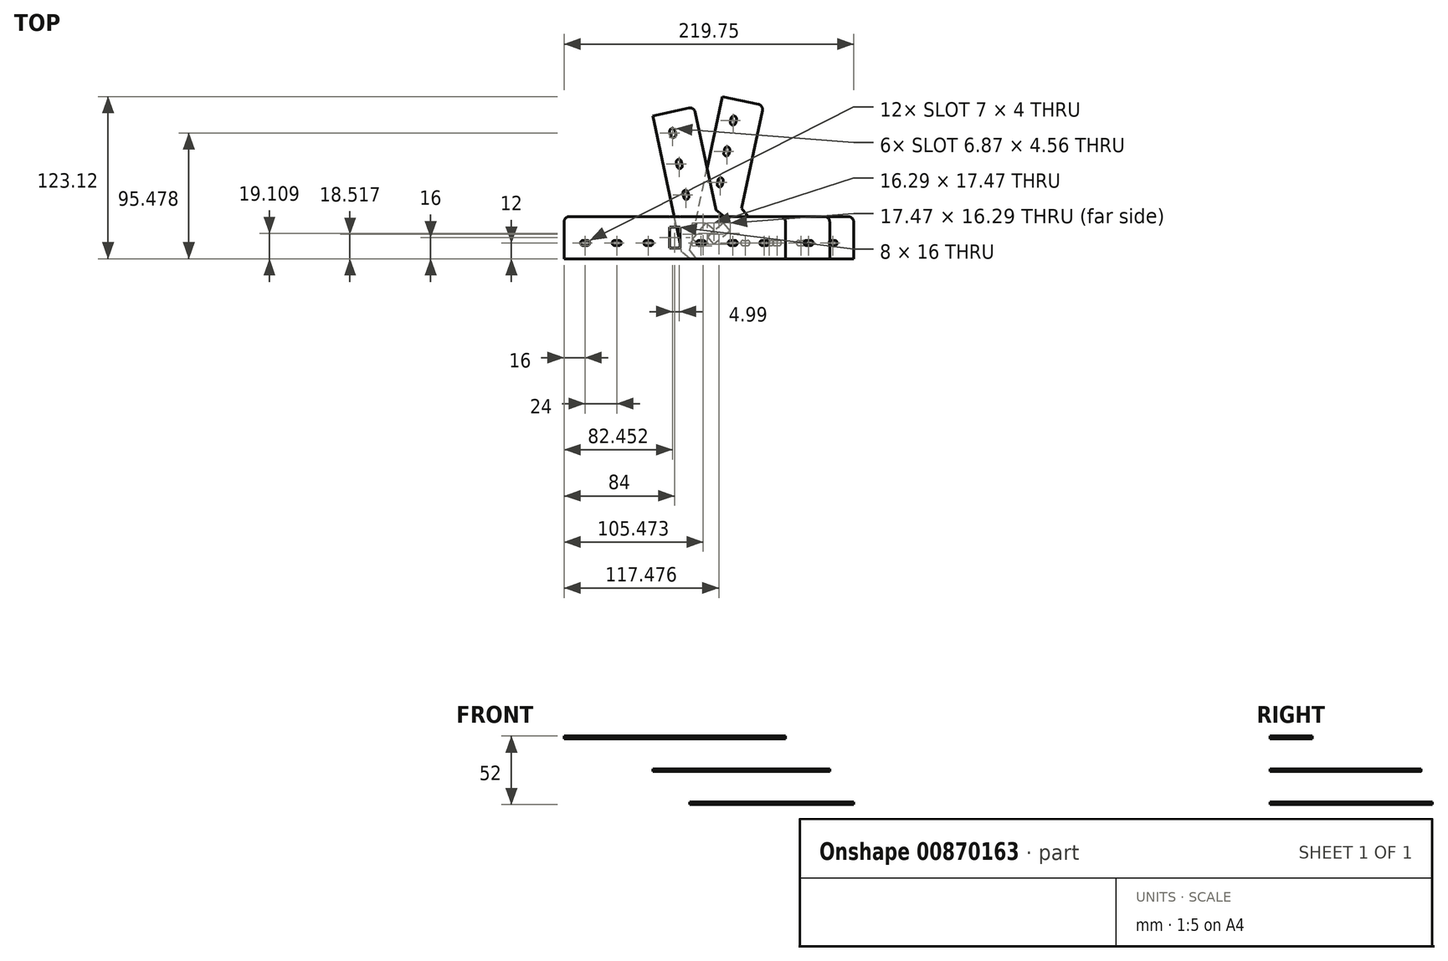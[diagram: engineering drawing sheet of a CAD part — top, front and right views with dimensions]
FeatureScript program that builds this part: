
annotation { "Feature Type Name" : "Feature", "Feature Type Description" : "" }
export const myFeature = defineFeature(function(context is Context, id is Id, definition is map)
    precondition{}
    {
        {
            var Q0;
            Q0=qCreatedBy(makeId("Top.planeOp"),FACE);
            var sketch = newSketch(context, id + "F0", { "sketchPlane" : qUnion([Q0])});
            skLineSegment(sketch, "E0", {"start": v(39.7, 32.14) * mm, "end": v(42.21, 29.03) * mm});
            skLineSegment(sketch, "E1", {"start": v(42.21, 29.03) * mm, "end": v(29.78, 18.97) * mm});
            skLineSegment(sketch, "E2", {"start": v(29.78, 18.97) * mm, "end": v(27.26, 22.07) * mm});
            skLineSegment(sketch, "E3", {"start": v(27.26, 22.07) * mm, "end": v(13.72, 11.1) * mm, "construction": true});
            skLineSegment(sketch, "E4", {"start": v(9.88, 8) * mm, "end": v(16.24, 8) * mm, "construction": true});
            skLineSegment(sketch, "E5", {"start": v(135.75, 8) * mm, "end": v(135.75, 36) * mm});
            skLineSegment(sketch, "E6", {"start": v(131.75, 40) * mm, "end": v(55.75, 40) * mm});
            skLineSegment(sketch, "E7", {"start": v(135.75, 8) * mm, "end": v(135.75, 0) * mm, "construction": true});
            skLineSegment(sketch, "E8", {"start": v(135.75, 0) * mm, "end": v(0, 0) * mm, "construction": true});
            skLineSegment(sketch, "E9", {"start": v(0, 0) * mm, "end": v(9.88, 8) * mm, "construction": true});
            skLineSegment(sketch, "E10", {"start": v(119.75, 40) * mm, "end": v(119.75, 0) * mm, "construction": true});
            skLineSegment(sketch, "E11", {"start": v(118.25, 22) * mm, "end": v(121.25, 22) * mm});
            skArc(sketch, "E12", {"start": v(118.25, 22) * mm, "mid": v(116.25, 20) * mm, "end": v(118.25, 18) * mm});
            skLineSegment(sketch, "E13", {"start": v(118.25, 18) * mm, "end": v(121.25, 18) * mm});
            skArc(sketch, "E14", {"start": v(121.25, 18) * mm, "mid": v(123.25, 20) * mm, "end": v(121.25, 22) * mm});
            skLineSegment(sketch, "E15", {"start": v(118.25, 20) * mm, "end": v(119.75, 20) * mm, "construction": true});
            skLineSegment(sketch, "E16", {"start": v(119.75, 20) * mm, "end": v(121.25, 20) * mm, "construction": true});
            skArc(sketch, "E17.1.0.0", {"start": v(94.25, 22) * mm, "mid": v(92.25, 20) * mm, "end": v(94.25, 18) * mm});
            skLineSegment(sketch, "E17.1.0.1", {"start": v(94.25, 22) * mm, "end": v(97.25, 22) * mm});
            skArc(sketch, "E17.1.0.2", {"start": v(97.25, 18) * mm, "mid": v(99.25, 20) * mm, "end": v(97.25, 22) * mm});
            skLineSegment(sketch, "E17.1.0.3", {"start": v(94.25, 18) * mm, "end": v(97.25, 18) * mm});
            skArc(sketch, "E17.2.0.0", {"start": v(70.25, 22) * mm, "mid": v(68.25, 20) * mm, "end": v(70.25, 18) * mm});
            skLineSegment(sketch, "E17.2.0.1", {"start": v(70.25, 22) * mm, "end": v(73.25, 22) * mm});
            skArc(sketch, "E17.2.0.2", {"start": v(73.25, 18) * mm, "mid": v(75.25, 20) * mm, "end": v(73.25, 22) * mm});
            skLineSegment(sketch, "E17.2.0.3", {"start": v(70.25, 18) * mm, "end": v(73.25, 18) * mm});
            skLineSegment(sketch, "E17.direction1", {"start": v(94.25, 18) * mm, "end": v(118.25, 18) * mm, "construction": true});
            skPoint(sketch, "E18.visualSharp", {"position": v(135.75, 40) * mm});
            skArc(sketch, "E18.filletArc", {"start": v(135.75, 36) * mm, "mid": v(134.58, 38.83) * mm, "end": v(131.75, 40) * mm});
            skLineSegment(sketch, "E19", {"start": v(53.23, 43.1) * mm, "end": v(39.7, 32.14) * mm, "construction": true});
            skLineSegment(sketch, "E20", {"start": v(0, 0) * mm, "end": v(2.05, 9.66) * mm, "construction": true});
            skLineSegment(sketch, "E21", {"start": v(2.05, 9.66) * mm, "end": v(9.88, 8) * mm, "construction": true});
            skLineSegment(sketch, "E22", {"start": v(9.88, 8) * mm, "end": v(9.88, 0) * mm, "construction": true});
            skLineSegment(sketch, "E23", {"start": v(9.88, 0) * mm, "end": v(0, 0) * mm, "construction": true});
            skLineSegment(sketch, "E24", {"start": v(16.24, 8) * mm, "end": v(13.72, 11.1) * mm});
            skLineSegment(sketch, "E25", {"start": v(16.24, 8) * mm, "end": v(135.75, 8) * mm});
            skLineSegment(sketch, "E26", {"start": v(13.72, 11.1) * mm, "end": v(9.88, 8) * mm, "construction": true});
            skLineSegment(sketch, "E27", {"start": v(55.75, 40) * mm, "end": v(53.23, 43.1) * mm});
            skLineSegment(sketch, "E28.MirrorCS", {"start": v(37.2, 88.45) * mm, "end": v(37.83, 91.38) * mm});
            skLineSegment(sketch, "E29.MirrorCS", {"start": v(41.12, 87.62) * mm, "end": v(41.74, 90.55) * mm});
            skLineSegment(sketch, "E30.MirrorCS", {"start": v(32.21, 64.97) * mm, "end": v(32.84, 67.9) * mm});
            skLineSegment(sketch, "E31.MirrorCS", {"start": v(42.2, 111.93) * mm, "end": v(42.82, 114.86) * mm});
            skLineSegment(sketch, "E32.MirrorCS", {"start": v(46.1, 111.1) * mm, "end": v(46.73, 114.03) * mm});
            skLineSegment(sketch, "E33.MirrorCS", {"start": v(36.13, 64.14) * mm, "end": v(36.75, 67.08) * mm});
            skArc(sketch, "E34.MirrorCS", {"start": v(37.83, 91.38) * mm, "mid": v(40.2, 92.92) * mm, "end": v(41.74, 90.55) * mm});
            skLineSegment(sketch, "E35.MirrorCS", {"start": v(24.74, 25.18) * mm, "end": v(27.26, 22.07) * mm});
            skArc(sketch, "E36.MirrorCS", {"start": v(41.12, 87.62) * mm, "mid": v(38.74, 86.08) * mm, "end": v(37.2, 88.45) * mm});
            skLineSegment(sketch, "E37.MirrorCS", {"start": v(36.05, 131.12) * mm, "end": v(63.44, 125.3) * mm});
            skPoint(sketch, "E38.MirrorP", {"position": v(67.35, 124.47) * mm});
            skLineSegment(sketch, "E39.MirrorCS", {"start": v(37.18, 35.25) * mm, "end": v(24.74, 25.18) * mm});
            skArc(sketch, "E40.MirrorCS", {"start": v(46.1, 111.1) * mm, "mid": v(43.73, 109.55) * mm, "end": v(42.2, 111.93) * mm});
            skLineSegment(sketch, "E41.MirrorCS", {"start": v(66.52, 120.56) * mm, "end": v(50.72, 46.22) * mm});
            skLineSegment(sketch, "E42.MirrorCS", {"start": v(11.2, 14.22) * mm, "end": v(13.72, 11.1) * mm});
            skLineSegment(sketch, "E43.MirrorCS", {"start": v(50.72, 46.22) * mm, "end": v(53.23, 43.1) * mm});
            skLineSegment(sketch, "E44.MirrorCS", {"start": v(11.2, 14.22) * mm, "end": v(36.05, 131.12) * mm});
            skArc(sketch, "E45.MirrorCS", {"start": v(63.44, 125.3) * mm, "mid": v(65.96, 123.57) * mm, "end": v(66.52, 120.56) * mm});
            skLineSegment(sketch, "E46.MirrorCS", {"start": v(39.7, 32.14) * mm, "end": v(37.18, 35.25) * mm});
            skArc(sketch, "E47.MirrorCS", {"start": v(36.13, 64.14) * mm, "mid": v(33.75, 62.6) * mm, "end": v(32.21, 64.97) * mm});
            skArc(sketch, "E48.MirrorCS", {"start": v(42.82, 114.86) * mm, "mid": v(45.19, 116.4) * mm, "end": v(46.73, 114.03) * mm});
            skArc(sketch, "E49.MirrorCS", {"start": v(32.84, 67.9) * mm, "mid": v(35.2, 69.45) * mm, "end": v(36.75, 67.08) * mm});
            skSolve(sketch);
        }
        {
            var Q0;
            Q0 = qSketchRegion(id + "F0", true);
            extrude(context, id + "F1", {"entities" : qUnion([Q0]), "depth" : 2 * mm, "offsetDistance" : 25 * mm});
        }
        {
            var Q0;
            Q0=qCreatedBy(makeId("Top.planeOp"),FACE);
            cPlane(context, id + "F2", {"entities" : qUnion([Q0]), "cplaneType" : CPlaneType.OFFSET, "offset" : 25 * mm, "width" : 150 * mm, "height" : 150 * mm});
        }
        {
            var Q0;
            Q0=qCreatedBy(id+"F2.planeOp",FACE);
            var sketch = newSketch(context, id + "F3", { "sketchPlane" : qUnion([Q0])});
            skLineSegment(sketch, "E50", {"start": v(0, 0) * mm, "end": v(117.54, 0) * mm, "construction": true});
            skLineSegment(sketch, "E51", {"start": v(117.54, 0) * mm, "end": v(117.54, 8) * mm, "construction": true});
            skLineSegment(sketch, "E52", {"start": v(11.63, 8) * mm, "end": v(8.52, 10.52) * mm});
            skLineSegment(sketch, "E53", {"start": v(11.63, 8) * mm, "end": v(117.54, 8) * mm});
            skLineSegment(sketch, "E54", {"start": v(117.54, 8) * mm, "end": v(117.54, 36) * mm});
            skArc(sketch, "E55", {"start": v(117.54, 36) * mm, "mid": v(116.37, 38.83) * mm, "end": v(113.54, 40) * mm});
            skLineSegment(sketch, "E56", {"start": v(113.54, 40) * mm, "end": v(37.54, 40) * mm});
            skLineSegment(sketch, "E57", {"start": v(37.54, 40) * mm, "end": v(34.43, 42.52) * mm});
            skLineSegment(sketch, "E58", {"start": v(34.43, 42.52) * mm, "end": v(26.5, 32.73) * mm, "construction": true});
            skLineSegment(sketch, "E59", {"start": v(26.5, 32.73) * mm, "end": v(29.62, 30.22) * mm});
            skLineSegment(sketch, "E60", {"start": v(29.62, 30.22) * mm, "end": v(19.55, 17.78) * mm});
            skLineSegment(sketch, "E61", {"start": v(19.55, 17.78) * mm, "end": v(16.44, 20.3) * mm});
            skLineSegment(sketch, "E62", {"start": v(16.44, 20.3) * mm, "end": v(8.52, 10.52) * mm, "construction": true});
            skLineSegment(sketch, "E63", {"start": v(8.52, 10.52) * mm, "end": v(6.48, 8) * mm, "construction": true});
            skLineSegment(sketch, "E64", {"start": v(6.48, 8) * mm, "end": v(0, 0) * mm, "construction": true});
            skLineSegment(sketch, "E65", {"start": v(0, 0) * mm, "end": v(-1.35, 6.34) * mm, "construction": true});
            skLineSegment(sketch, "E66", {"start": v(-1.35, 6.34) * mm, "end": v(6.48, 8) * mm, "construction": true});
            skLineSegment(sketch, "E67", {"start": v(6.48, 8) * mm, "end": v(6.48, 0) * mm, "construction": true});
            skLineSegment(sketch, "E68", {"start": v(6.48, 0) * mm, "end": v(0, 0) * mm, "construction": true});
            skLineSegment(sketch, "E69", {"start": v(101.54, 0) * mm, "end": v(101.54, 40) * mm, "construction": true});
            skLineSegment(sketch, "E70", {"start": v(101.54, 20) * mm, "end": v(100.04, 20) * mm, "construction": true});
            skLineSegment(sketch, "E71", {"start": v(101.54, 20) * mm, "end": v(103.04, 20) * mm, "construction": true});
            skArc(sketch, "E72", {"start": v(100.04, 18) * mm, "mid": v(98.04, 20) * mm, "end": v(100.04, 22) * mm});
            skArc(sketch, "E73", {"start": v(103.04, 22) * mm, "mid": v(105.04, 20) * mm, "end": v(103.04, 18) * mm});
            skLineSegment(sketch, "E74", {"start": v(100.04, 22) * mm, "end": v(103.04, 22) * mm});
            skLineSegment(sketch, "E75", {"start": v(100.04, 18) * mm, "end": v(103.04, 18) * mm});
            skArc(sketch, "E76.1.0.0", {"start": v(76.04, 18) * mm, "mid": v(74.04, 20) * mm, "end": v(76.04, 22) * mm});
            skLineSegment(sketch, "E76.1.0.1", {"start": v(76.04, 22) * mm, "end": v(79.04, 22) * mm});
            skArc(sketch, "E76.1.0.2", {"start": v(79.04, 22) * mm, "mid": v(81.04, 20) * mm, "end": v(79.04, 18) * mm});
            skLineSegment(sketch, "E76.1.0.3", {"start": v(76.04, 18) * mm, "end": v(79.04, 18) * mm});
            skArc(sketch, "E76.2.0.0", {"start": v(52.04, 18) * mm, "mid": v(50.04, 20) * mm, "end": v(52.04, 22) * mm});
            skLineSegment(sketch, "E76.2.0.1", {"start": v(52.04, 22) * mm, "end": v(55.04, 22) * mm});
            skArc(sketch, "E76.2.0.2", {"start": v(55.04, 22) * mm, "mid": v(57.04, 20) * mm, "end": v(55.04, 18) * mm});
            skLineSegment(sketch, "E76.2.0.3", {"start": v(52.04, 18) * mm, "end": v(55.04, 18) * mm});
            skLineSegment(sketch, "E76.direction1", {"start": v(100.04, 18) * mm, "end": v(76.04, 18) * mm, "construction": true});
            skLineSegment(sketch, "E77.MirrorCS", {"start": v(5.4, 13.03) * mm, "end": v(8.52, 10.52) * mm});
            skLineSegment(sketch, "E78.MirrorCS", {"start": v(-3.2, 101.6) * mm, "end": v(-3.82, 104.53) * mm});
            skLineSegment(sketch, "E79.MirrorCS", {"start": v(6.79, 54.64) * mm, "end": v(6.16, 57.58) * mm});
            skLineSegment(sketch, "E80.MirrorCS", {"start": v(10.7, 55.48) * mm, "end": v(10.08, 58.4) * mm});
            skLineSegment(sketch, "E81.MirrorCS", {"start": v(1.8, 78.12) * mm, "end": v(1.17, 81.05) * mm});
            skLineSegment(sketch, "E82.MirrorCS", {"start": v(0.72, 102.43) * mm, "end": v(0.1, 105.36) * mm});
            skLineSegment(sketch, "E83.MirrorCS", {"start": v(5.7, 78.95) * mm, "end": v(5.09, 81.89) * mm});
            skLineSegment(sketch, "E84.MirrorCS", {"start": v(13.33, 22.82) * mm, "end": v(16.44, 20.3) * mm});
            skLineSegment(sketch, "E85.MirrorCS", {"start": v(26.5, 32.73) * mm, "end": v(23.4, 35.25) * mm});
            skLineSegment(sketch, "E86.MirrorCS", {"start": v(31.32, 45.03) * mm, "end": v(34.43, 42.52) * mm});
            skArc(sketch, "E87.MirrorCS", {"start": v(0.1, 105.36) * mm, "mid": v(-2.28, 106.9) * mm, "end": v(-3.82, 104.53) * mm});
            skArc(sketch, "E88.MirrorCS", {"start": v(5.09, 81.89) * mm, "mid": v(2.71, 83.43) * mm, "end": v(1.17, 81.05) * mm});
            skArc(sketch, "E89.MirrorCS", {"start": v(10.78, 122.45) * mm, "mid": v(13.79, 121.9) * mm, "end": v(15.52, 119.37) * mm});
            skArc(sketch, "E90.MirrorCS", {"start": v(6.79, 54.64) * mm, "mid": v(9.16, 53.1) * mm, "end": v(10.7, 55.48) * mm});
            skLineSegment(sketch, "E91.MirrorCS", {"start": v(15.52, 119.37) * mm, "end": v(31.32, 45.03) * mm});
            skArc(sketch, "E92.MirrorCS", {"start": v(1.8, 78.12) * mm, "mid": v(4.17, 76.58) * mm, "end": v(5.7, 78.95) * mm});
            skLineSegment(sketch, "E93.MirrorCS", {"start": v(5.4, 13.03) * mm, "end": v(-16.61, 116.63) * mm});
            skLineSegment(sketch, "E94.MirrorCS", {"start": v(-16.61, 116.63) * mm, "end": v(10.78, 122.45) * mm});
            skLineSegment(sketch, "E95.MirrorCS", {"start": v(23.4, 35.25) * mm, "end": v(13.33, 22.82) * mm});
            skArc(sketch, "E96.MirrorCS", {"start": v(10.08, 58.4) * mm, "mid": v(7.7, 59.95) * mm, "end": v(6.16, 57.58) * mm});
            skArc(sketch, "E97.MirrorCS", {"start": v(-3.2, 101.6) * mm, "mid": v(-0.82, 100.05) * mm, "end": v(0.72, 102.43) * mm});
            skSolve(sketch);
        }
        {
            var Q0;
            Q0 = qSketchRegion(id + "F3", true);
            extrude(context, id + "F4", {"entities" : qUnion([Q0]), "depth" : 2 * mm, "offsetDistance" : 25 * mm});
        }
        {
            var Q0;
            Q0=qCreatedBy(id+"F2.planeOp",FACE);
            cPlane(context, id + "F5", {"entities" : qUnion([Q0]), "cplaneType" : CPlaneType.OFFSET, "offset" : 25 * mm, "width" : 150 * mm, "height" : 150 * mm});
        }
        {
            var Q0;
            Q0=qCreatedBy(id+"F5.planeOp",FACE);
            var sketch = newSketch(context, id + "F6", { "sketchPlane" : qUnion([Q0])});
            skLineSegment(sketch, "E98", {"start": v(0, 0) * mm, "end": v(84, 0) * mm, "construction": true});
            skLineSegment(sketch, "E99", {"start": v(84, 0) * mm, "end": v(84, 8) * mm, "construction": true});
            skLineSegment(sketch, "E100", {"start": v(84, 8) * mm, "end": v(4, 8) * mm});
            skLineSegment(sketch, "E101", {"start": v(4, 8) * mm, "end": v(0, 8) * mm});
            skLineSegment(sketch, "E102", {"start": v(0, 8) * mm, "end": v(0, 16) * mm, "construction": true});
            skLineSegment(sketch, "E103", {"start": v(0, 16) * mm, "end": v(4, 16) * mm});
            skLineSegment(sketch, "E104", {"start": v(4, 16) * mm, "end": v(4, 32) * mm});
            skLineSegment(sketch, "E105", {"start": v(4, 32) * mm, "end": v(0, 32) * mm});
            skLineSegment(sketch, "E106", {"start": v(0, 32) * mm, "end": v(0, 40) * mm, "construction": true});
            skLineSegment(sketch, "E107", {"start": v(0, 40) * mm, "end": v(3.5, 40) * mm});
            skArc(sketch, "E108", {"start": v(84, 36) * mm, "mid": v(82.83, 38.83) * mm, "end": v(80, 40) * mm});
            skLineSegment(sketch, "E109", {"start": v(84, 36) * mm, "end": v(84, 8) * mm});
            skLineSegment(sketch, "E110", {"start": v(68, 0) * mm, "end": v(68, 40) * mm, "construction": true});
            skLineSegment(sketch, "E111", {"start": v(68, 20) * mm, "end": v(66.5, 20) * mm, "construction": true});
            skLineSegment(sketch, "E112", {"start": v(68, 20) * mm, "end": v(69.5, 20) * mm, "construction": true});
            skArc(sketch, "E113", {"start": v(66.5, 22) * mm, "mid": v(64.5, 20) * mm, "end": v(66.5, 18) * mm});
            skArc(sketch, "E114", {"start": v(69.5, 22) * mm, "mid": v(71.5, 20) * mm, "end": v(69.5, 18) * mm});
            skLineSegment(sketch, "E115", {"start": v(66.5, 22) * mm, "end": v(69.5, 22) * mm});
            skLineSegment(sketch, "E116", {"start": v(69.5, 18) * mm, "end": v(66.5, 18) * mm});
            skArc(sketch, "E117.1.0.0", {"start": v(42.5, 22) * mm, "mid": v(40.5, 20) * mm, "end": v(42.5, 18) * mm});
            skLineSegment(sketch, "E117.1.0.1", {"start": v(42.5, 22) * mm, "end": v(45.5, 22) * mm});
            skArc(sketch, "E117.1.0.2", {"start": v(45.5, 22) * mm, "mid": v(47.5, 20) * mm, "end": v(45.5, 18) * mm});
            skLineSegment(sketch, "E117.1.0.3", {"start": v(45.5, 18) * mm, "end": v(42.5, 18) * mm});
            skArc(sketch, "E117.2.0.0", {"start": v(18.5, 22) * mm, "mid": v(16.5, 20) * mm, "end": v(18.5, 18) * mm});
            skLineSegment(sketch, "E117.2.0.1", {"start": v(18.5, 22) * mm, "end": v(21.5, 22) * mm});
            skArc(sketch, "E117.2.0.2", {"start": v(21.5, 22) * mm, "mid": v(23.5, 20) * mm, "end": v(21.5, 18) * mm});
            skLineSegment(sketch, "E117.2.0.3", {"start": v(21.5, 18) * mm, "end": v(18.5, 18) * mm});
            skLineSegment(sketch, "E117.direction1", {"start": v(66.5, 18) * mm, "end": v(42.5, 18) * mm, "construction": true});
            skLineSegment(sketch, "E118", {"start": v(4.5, 40) * mm, "end": v(4, 39.5) * mm});
            skLineSegment(sketch, "E119", {"start": v(4, 39.5) * mm, "end": v(3.5, 40) * mm});
            skLineSegment(sketch, "E120", {"start": v(4.5, 40) * mm, "end": v(80, 40) * mm});
            skPoint(sketch, "E121.start.orphan", {"position": v(4, 40) * mm});
            skLineSegment(sketch, "E122.MirrorCS", {"start": v(-4.5, 40) * mm, "end": v(-4, 39.5) * mm});
            skLineSegment(sketch, "E123.MirrorCS", {"start": v(-4, 39.5) * mm, "end": v(-3.5, 40) * mm});
            skLineSegment(sketch, "E124.MirrorCS", {"start": v(-69.5, 18) * mm, "end": v(-66.5, 18) * mm});
            skLineSegment(sketch, "E125.MirrorCS", {"start": v(-21.5, 18) * mm, "end": v(-18.5, 18) * mm});
            skLineSegment(sketch, "E126.MirrorCS", {"start": v(-18.5, 22) * mm, "end": v(-21.5, 22) * mm});
            skLineSegment(sketch, "E127.MirrorCS", {"start": v(-42.5, 22) * mm, "end": v(-45.5, 22) * mm});
            skLineSegment(sketch, "E128.MirrorCS", {"start": v(-45.5, 18) * mm, "end": v(-42.5, 18) * mm});
            skLineSegment(sketch, "E129.MirrorCS", {"start": v(0, 40) * mm, "end": v(-3.5, 40) * mm});
            skLineSegment(sketch, "E130.MirrorCS", {"start": v(-4, 32) * mm, "end": v(0, 32) * mm});
            skLineSegment(sketch, "E131.MirrorCS", {"start": v(-4, 8) * mm, "end": v(0, 8) * mm});
            skLineSegment(sketch, "E132.MirrorCS", {"start": v(-66.5, 22) * mm, "end": v(-69.5, 22) * mm});
            skLineSegment(sketch, "E133.MirrorCS", {"start": v(0, 16) * mm, "end": v(-4, 16) * mm});
            skArc(sketch, "E134.MirrorCS", {"start": v(-69.5, 22) * mm, "mid": v(-71.5, 20) * mm, "end": v(-69.5, 18) * mm});
            skArc(sketch, "E135.MirrorCS", {"start": v(-45.5, 22) * mm, "mid": v(-47.5, 20) * mm, "end": v(-45.5, 18) * mm});
            skLineSegment(sketch, "E136.MirrorCS", {"start": v(-84, 8) * mm, "end": v(-4, 8) * mm});
            skLineSegment(sketch, "E137.MirrorCS", {"start": v(-84, 36) * mm, "end": v(-84, 8) * mm});
            skArc(sketch, "E138.MirrorCS", {"start": v(-42.5, 22) * mm, "mid": v(-40.5, 20) * mm, "end": v(-42.5, 18) * mm});
            skLineSegment(sketch, "E139.MirrorCS", {"start": v(-4.5, 40) * mm, "end": v(-80, 40) * mm});
            skLineSegment(sketch, "E140.MirrorCS", {"start": v(-4, 16) * mm, "end": v(-4, 32) * mm});
            skArc(sketch, "E141.MirrorCS", {"start": v(-18.5, 22) * mm, "mid": v(-16.5, 20) * mm, "end": v(-18.5, 18) * mm});
            skPoint(sketch, "E142.MirrorP", {"position": v(-4, 40) * mm});
            skArc(sketch, "E143.MirrorCS", {"start": v(-84, 36) * mm, "mid": v(-82.83, 38.83) * mm, "end": v(-80, 40) * mm});
            skArc(sketch, "E144.MirrorCS", {"start": v(-21.5, 22) * mm, "mid": v(-23.5, 20) * mm, "end": v(-21.5, 18) * mm});
            skArc(sketch, "E145.MirrorCS", {"start": v(-66.5, 22) * mm, "mid": v(-64.5, 20) * mm, "end": v(-66.5, 18) * mm});
            skSolve(sketch);
        }
        {
            var Q0;
            Q0 = qSketchRegion(id + "F6", true);
            extrude(context, id + "F7", {"entities" : qUnion([Q0]), "depth" : 2 * mm, "offsetDistance" : 25 * mm});
        }
    });
